MODEL slx_5cf3387b0fd6
CONFIG AbsTol = auto
CONFIG EnableMultiTasking = off
CONFIG FixedStep = 1e-3
CONFIG MaxStep = auto
CONFIG MinStep = auto
CONFIG RelTol = 1e-3
CONFIG SampleTimeConstraint = Unconstrained
CONFIG Solver = ode14x
CONFIG SolverName = ode14x
CONFIG StartTime = 0.0
CONFIG StopTime = 15
BLOCK [From] Actual ouput1
  GotoTag = Y
BLOCK [Sum] Add2
  IconShape = rectangular
  Ports = [2, 1]
BLOCK [From] Disturbance Input1
  GotoTag = D
BLOCK [From] Error1
  GotoTag = E
BLOCK [Gain] Force to Voltage
  Gain = 1/ 2871.14
BLOCK [FromWorkspace] From Workspace1
  OutDataTypeStr = double
  OutputAfterFinalValue = Setting to zero
  VariableName = Cut1500down
BLOCK [Goto] Goto4
  GotoTag = D
BLOCK [Goto] Goto5
  GotoTag = R
BLOCK [Goto] Goto6
  GotoTag = E
BLOCK [Goto] Goto7
  GotoTag = Y
BLOCK [Integrator] Integrator2
  InitialCondition = .1
  Ports = [1, 1]
BLOCK [Gain] K_i
  Gain = gain_V_I
BLOCK [Gain] K_p
  Gain = gain_P
BLOCK [Gain] K_v
  Gain = gain_V_P
BLOCK [ManualSwitch] Manual Switch1
  NameLocation = left
BLOCK [Scope] Output Position (mm)
  Floating = off
  NumInputPorts = 1
  Ports = [1]
  ScopeSpecificationString = Simulink.scopes.TimeScopeBlockCfg('CurrentConfiguration', extmgr.ConfigurationSet(extmgr.Configuration('Core','General UI',true),extmgr.Configuration('Core','Source UI',true),extmgr.Configuration('Sources','WiredSimulink',true,'DataLoggingVariableName','ScopeData2'),extmgr.Configuration('Visuals','Time Domain',true,'SerializedDisplays',{struct('MinYLimReal','-66692021064882830098913468871871206665...<+3796ch>
BLOCK [TransferFcn] Plant (Googol Tech)
  Denominator = [1 163 193.3]
  Numerator = [78020]
BLOCK [Sin] Ref. Position, Xref (mm)
  Amplitude = 5
  Frequency = 0.5*(2*pi)
  Offset = 1/2000
  Ports = [0, 1]
  SampleTime = 0
BLOCK [From] Reference Input1
  GotoTag = R
BLOCK [Saturate] Saturation1
  LowerLimit = -92
  UpperLimit = 92
BLOCK [Scope] Scope1
  Floating = off
  NumInputPorts = 4
  Ports = [4]
  ScopeSpecificationString = Simulink.scopes.TimeScopeBlockCfg('CurrentConfiguration', extmgr.ConfigurationSet(extmgr.Configuration('Core','General UI',true),extmgr.Configuration('Core','Source UI',true),extmgr.Configuration('Sources','WiredSimulink',true,'DataLoggingVariableName','ScopeData3','DataLogging',true,'DataLoggingSaveFormat','StructureWithTime'),extmgr.Configuration('Visuals','Time Domain',true,'SerializedDisplays'...<+3907ch>
BLOCK [Sum] Sum2
  Inputs = ++|
  Ports = [2, 1]
BLOCK [Sum] Sum5
  Inputs = |+-
  NameLocation = top
  Ports = [2, 1]
BLOCK [Sum] Sum6
  Inputs = |+-
  NameLocation = top
  Ports = [2, 1]
BLOCK [TransportDelay] TIme Delay
  DelayTime = 0.0012
  Ports = [1, 1]
BLOCK [TransferFcn] V est
  Denominator = [1 942.5]
  Numerator = [942.5, 0]
LINE Actual ouput1:1 -> Scope1:4
LINE Add2:1 -> Sum2:2
LINE Disturbance Input1:1 -> Scope1:1
LINE Error1:1 -> Scope1:2
LINE Force to Voltage:1 -> Goto4:1
LINE Force to Voltage:1 -> Manual Switch1:1
LINE From Workspace1:1 -> Force to Voltage:1
LINE Integrator2:1 -> Add2:2
LINE K_i:1 -> Integrator2:1
LINE K_p:1 -> Sum5:1
LINE K_v:1 -> Add2:1
LINE Manual Switch1:1 -> Sum2:1
LINE Plant (Googol Tech):1 -> TIme Delay:1
LINE Ref. Position, Xref (mm):1 -> Goto5:1
LINE Ref. Position, Xref (mm):1 -> Sum6:1
LINE Reference Input1:1 -> Scope1:3
LINE Saturation1:1 -> Plant (Googol Tech):1
LINE Sum2:1 -> Saturation1:1
LINE Sum5:1 -> K_i:1
LINE Sum5:1 -> K_v:1
LINE Sum6:1 -> Goto6:1
LINE Sum6:1 -> K_p:1
LINE TIme Delay:1 -> Goto7:1
LINE TIme Delay:1 -> Output Position (mm):1
LINE TIme Delay:1 -> Sum6:2
LINE TIme Delay:1 -> V est:1
LINE V est:1 -> Sum5:2
